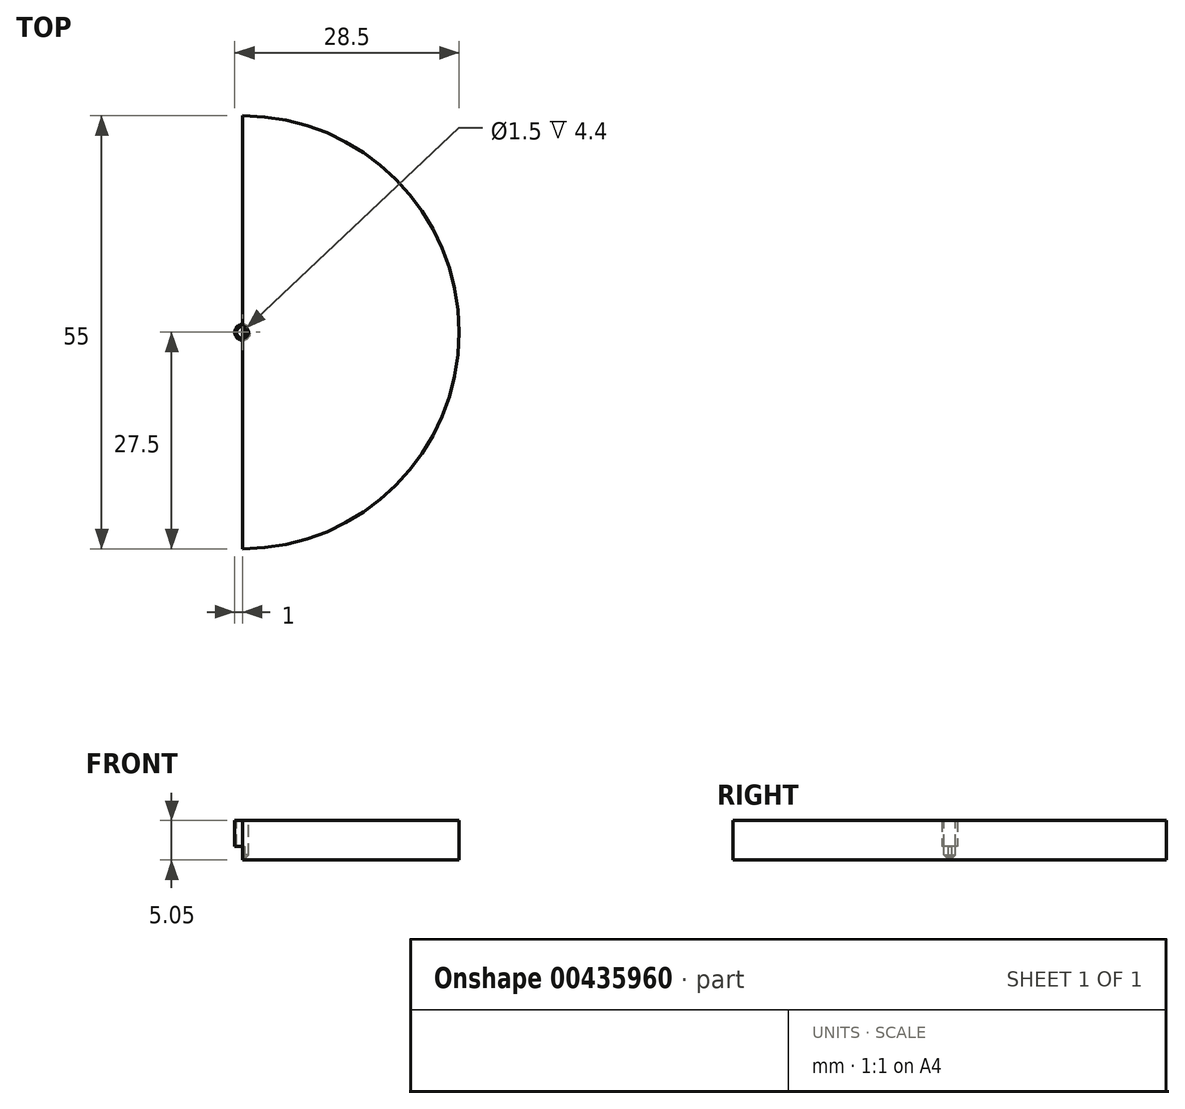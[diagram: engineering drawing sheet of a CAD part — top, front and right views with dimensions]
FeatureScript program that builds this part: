
annotation { "Feature Type Name" : "Feature", "Feature Type Description" : "" }
export const myFeature = defineFeature(function(context is Context, id is Id, definition is map)
    precondition{}
    {
        {
            var Q0;
            Q0=qCreatedBy(makeId("Top.planeOp"),FACE);
            var sketch = newSketch(context, id + "F0", { "sketchPlane" : qUnion([Q0])});
            skCircle(sketch, "E0", {"center": v(0, 0) * mm, "radius": 27.5 * mm});
            skSolve(sketch);
        }
        {
            var Q0;
            Q0=makeQuery(id+"F0.imprint","IMPRINT",FACE,{"disambiguationData":[TD([[makeQuery(id+"F0.imprint","IMPRINT",EDGE,{"derivedFrom":sQuery(id+"F0.wireOp",EDGE,"E0")}),1.0]])]});
            extrude(context, id + "F1", {"entities" : qUnion([Q0]), "depth" : 5 * mm});
        }
        {
            var Q0;
            Q0=makeQuery(id+"F1.opExtrude","CAP_FACE",FACE,{"disambiguationData":[OSD([sQuery(id+"F0.wireOp",EDGE,"E0")])],"isStart":false});
            var sketch = newSketch(context, id + "F2", { "sketchPlane" : qUnion([Q0])});
            skCircle(sketch, "E1", {"center": v(0, 0) * mm, "radius": 0.75 * mm});
            skSolve(sketch);
        }
        {
            var Q0;
            Q0 = qSketchRegion(id + "F2", true);
            extrude(context, id + "F3", {"entities" : qUnion([Q0]), "operationType" : NewBodyOperationType.REMOVE, "oppositeDirection" : true, "depth" : 4.65 * mm});
        }
        {
            var Q0;
            Q0=makeQuery(id+"F3.boolean.opBoolean","COPY",FACE,{"derivedFrom":makeQuery(id+"F3.opExtrude","CAP_FACE",FACE,{"disambiguationData":[OSD([sQuery(id+"F2.wireOp",EDGE,"E1")])],"isStart":false})});
            var sketch = newSketch(context, id + "F4", { "sketchPlane" : qUnion([Q0])});
            skCircle(sketch, "E2", {"center": v(0, 0) * mm, "radius": 0.25 * mm});
            skSolve(sketch);
        }
        {
            var Q0;
            Q0 = qSketchRegion(id + "F4", true);
            extrude(context, id + "F5", {"entities" : qUnion([Q0]), "operationType" : NewBodyOperationType.ADD, "depth" : 1.35 * mm});
        }
        {
            var Q0;
            Q0=makeQuery(id+"F3.boolean.opBoolean","COPY",EDGE,{"derivedFrom":makeQuery(id+"F3.opExtrude","CAP_EDGE",EDGE,{"disambiguationData":[OSD([sQuery(id+"F2.wireOp",EDGE,"E1")])],"isStart":false})});
            chamfer(context, id + "F6", {"entities" : qUnion([Q0]), "width" : 0.25 * mm, "tangentPropagation" : true});
        }
        {
            var Q0;
            Q0=makeQuery(id+"F1.opExtrude","CAP_FACE",FACE,{"disambiguationData":[OSD([sQuery(id+"F0.wireOp",EDGE,"E0")])],"isStart":true});
            var sketch = newSketch(context, id + "F7", { "sketchPlane" : qUnion([Q0])});
            skCircle(sketch, "E3", {"center": v(0, 0) * mm, "radius": 1 * mm});
            skSolve(sketch);
        }
        {
            var Q0;
            Q0 = qSketchRegion(id + "F7", true);
            extrude(context, id + "F8", {"entities" : qUnion([Q0]), "operationType" : NewBodyOperationType.ADD, "depth" : 0.05 * mm});
        }
        {
            var Q0;
            Q0=makeQuery(id+"F8.opExtrude","CAP_FACE",FACE,{"disambiguationData":[OSD([sQuery(id+"F7.wireOp",EDGE,"E3")])],"isStart":false});
            var sketch = newSketch(context, id + "F9", { "sketchPlane" : qUnion([Q0])});
            skLineSegment(sketch, "E4.bottom", {"start": v(0, 29.6) * mm, "end": v(-29.54, 29.6) * mm});
            skLineSegment(sketch, "E4.top", {"start": v(0, -30.94) * mm, "end": v(-29.54, -30.94) * mm});
            skLineSegment(sketch, "E4.left", {"start": v(0, 29.6) * mm, "end": v(0, -30.94) * mm});
            skLineSegment(sketch, "E4.right", {"start": v(-29.54, 29.6) * mm, "end": v(-29.54, -30.94) * mm});
            skSolve(sketch);
        }
        {
            var Q0;
            {var subQ4=sQuery(id+"F9.wireOp",EDGE,"E4.bottom");Q0=makeQuery(id+"F9.imprint","IMPRINT",FACE,{"disambiguationData":[TD([[makeQuery(id+"F9.imprint","IMPRINT",EDGE,{"derivedFrom":subQ4}),1.0]])]});}
            extrude(context, id + "F10", {"entities" : qUnion([Q0]), "operationType" : NewBodyOperationType.REMOVE, "oppositeDirection" : true, "depth" : 65.3 * mm});
        }
        {
            var Q0;
            Q0=makeQuery(id+"F5.opExtrude","CAP_FACE",FACE,{"disambiguationData":[OSD([sQuery(id+"F4.wireOp",EDGE,"E2")])],"isStart":false});
            var sketch = newSketch(context, id + "F11", { "sketchPlane" : qUnion([Q0])});
            skLineSegment(sketch, "E5.bottom", {"start": v(0, 1.56) * mm, "end": v(-1.62, 1.56) * mm});
            skLineSegment(sketch, "E5.top", {"start": v(0, -1.66) * mm, "end": v(-1.62, -1.66) * mm});
            skLineSegment(sketch, "E5.left", {"start": v(0, 1.56) * mm, "end": v(0, -1.66) * mm});
            skLineSegment(sketch, "E5.right", {"start": v(-1.62, 1.56) * mm, "end": v(-1.62, -1.66) * mm});
            skSolve(sketch);
        }
        {
            var Q0;
            Q0 = qSketchRegion(id + "F11", true);
            extrude(context, id + "F12", {"entities" : qUnion([Q0]), "operationType" : NewBodyOperationType.REMOVE, "oppositeDirection" : true, "depth" : 53.4 * mm});
        }
    });
